# Revit family: Sanitary_Toilets_Johnson-Suisse_Venezia_FTW_Suite
name_source: partatom
category: Plumbing Fixtures
revit_build: Autodesk Revit 2015 (Build: 20140606_1530(x64)
units: mm (PartAtom-declared; Revit-internal decimal feet)

## types (1)
- Venezia FTW Suite
    BIMobject category = Toilets
    Brand url = http://www.johnsonsuisse.com.au
    Design country = Spain
    EAN code = https://9325304005171
    Edition number = 1
    IFC Classification = Sanitary Terminal
    Manufacturer country = China
    Manufacturer name = Johnson Suisse
    Material main = Vitreous china
    NBS Reference Code = 35-65-90
    NBS Reference Description = Toilet Systems
    Nominal height = 781 mm  [stored 2.56234 ft]
    Nominal width = 390 mm  [stored 1.27953 ft]
    Product Guid = 6abbdcf7-470a-40ff-88dc-e3eed8086c42
    Product SKU = J2320_J2371_X011H
    Product data url = https://bimobject.com
    Product family = Venezia
    Product group = Toilets
    Product url = https://johnsonsuisse.com.au
    QR code = http://bimobject.com
    Technical description = https://johnsonsuisse.com.au
    Type = venezia_ftw_suite : Default
    UNSPSC Code = 301815
    Uniclass 1.4 Code = L7216
    Uniclass 1.4 Description = Toilets
    Uniclass 2.0 Code = SS-35-65-90
    Uniclass 2.0 Description = Toilet Systems
    Uniclass 2015 Code = SL_35_80_89
    Uniclass 2015 Name = Toilets
    Weight Net (Kg) = 0

note: [stored X ft] marks values corroborated as IEEE doubles in the binary element streams (Revit-internal decimal feet)

## geometry (parser evidence)
native form markers: Sweep x3
no freeform markers — native parametric forms only
